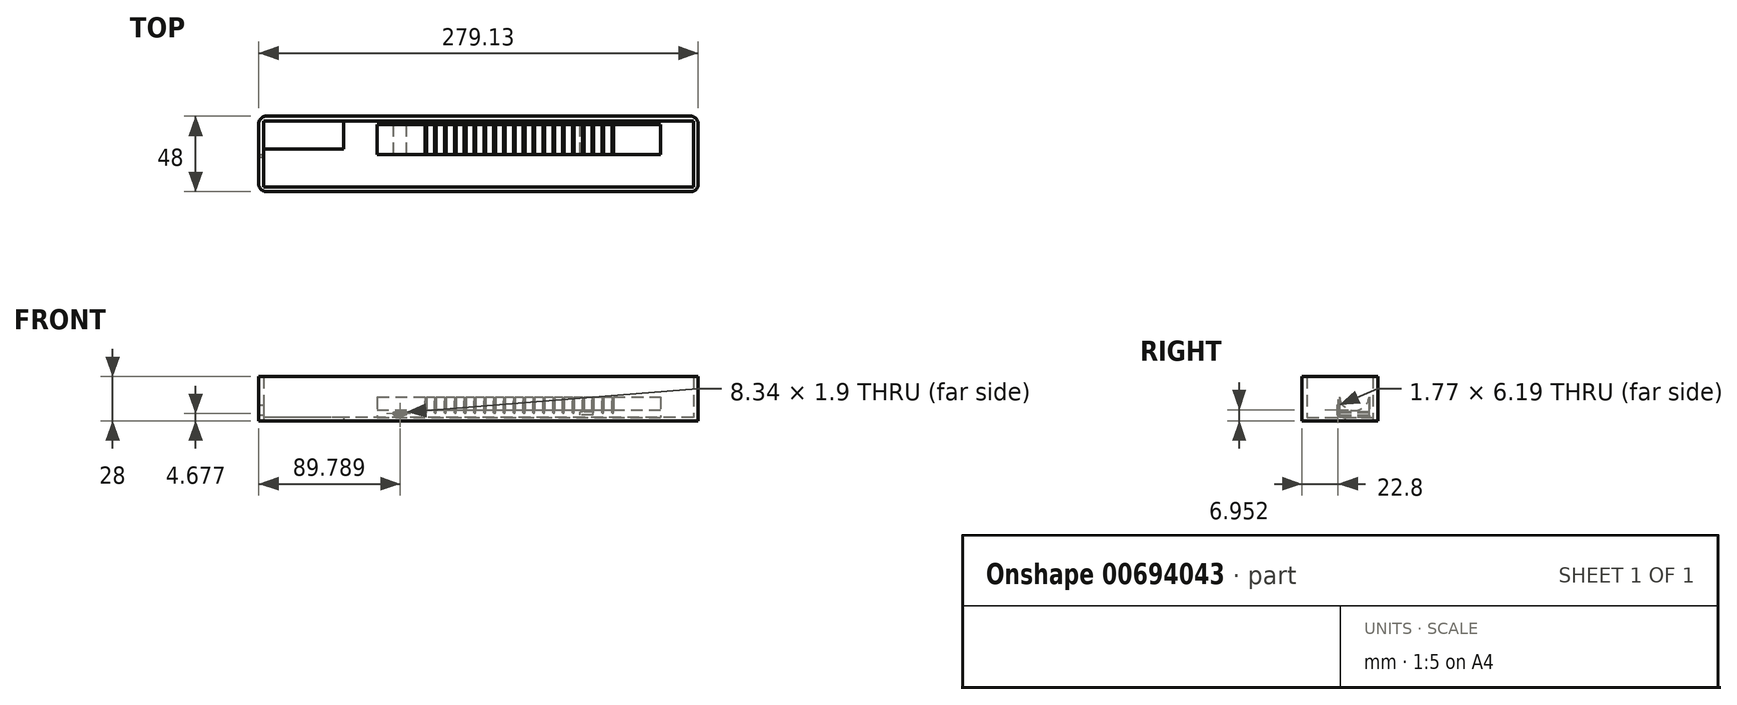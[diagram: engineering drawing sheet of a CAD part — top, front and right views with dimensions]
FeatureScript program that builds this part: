
annotation { "Feature Type Name" : "Feature", "Feature Type Description" : "" }
export const myFeature = defineFeature(function(context is Context, id is Id, definition is map)
    precondition{}
    {
        {
            var Q0;
            Q0=qCreatedBy(makeId("Top.planeOp"),FACE);
            var sketch = newSketch(context, id + "F0", { "sketchPlane" : qUnion([Q0])});
            skLineSegment(sketch, "E0.bottom", {"start": v(127.12, -24) * mm, "end": v(-146.01, -24) * mm});
            skLineSegment(sketch, "E0.top", {"start": v(127.12, 18) * mm, "end": v(-146.01, 18) * mm});
            skLineSegment(sketch, "E0.left", {"start": v(127.12, -24) * mm, "end": v(127.12, 18) * mm});
            skLineSegment(sketch, "E0.right", {"start": v(-146.01, -24) * mm, "end": v(-146.01, 18) * mm});
            skPoint(sketch, "E0.middle", {"position": v(0, 0) * mm});
            skLineSegment(sketch, "E1.bottom", {"start": v(-140.46, 74.6) * mm, "end": v(-84.46, 74.6) * mm});
            skLineSegment(sketch, "E1.top", {"start": v(-140.46, 108.6) * mm, "end": v(-84.46, 108.6) * mm});
            skLineSegment(sketch, "E1.left", {"start": v(-140.46, 74.6) * mm, "end": v(-140.46, 108.6) * mm});
            skLineSegment(sketch, "E1.right", {"start": v(-84.46, 74.6) * mm, "end": v(-84.46, 108.6) * mm});
            skLineSegment(sketch, "E2.0", {"start": v(-143.46, 111.6) * mm, "end": v(-81.46, 111.6) * mm, "construction": true});
            skLineSegment(sketch, "E2.1", {"start": v(-143.46, 71.6) * mm, "end": v(-143.46, 111.6) * mm, "construction": true});
            skLineSegment(sketch, "E2.2", {"start": v(-143.46, 71.6) * mm, "end": v(-81.46, 71.6) * mm, "construction": true});
            skLineSegment(sketch, "E2.3", {"start": v(-81.46, 71.6) * mm, "end": v(-81.46, 111.6) * mm, "construction": true});
            skLineSegment(sketch, "E3.bottom", {"start": v(-73.68, 15.64) * mm, "end": v(106.32, 15.64) * mm});
            skLineSegment(sketch, "E3.top", {"start": v(-73.68, -3.36) * mm, "end": v(106.32, -3.36) * mm});
            skLineSegment(sketch, "E3.left", {"start": v(-73.68, 15.64) * mm, "end": v(-73.68, -3.36) * mm});
            skLineSegment(sketch, "E3.right", {"start": v(106.32, 15.64) * mm, "end": v(106.32, -3.36) * mm});
            skLineSegment(sketch, "E4.bottom", {"start": v(96.3, 104.7) * mm, "end": v(145.3, 104.7) * mm, "construction": true});
            skLineSegment(sketch, "E4.top", {"start": v(96.3, 78.7) * mm, "end": v(145.3, 78.7) * mm, "construction": true});
            skLineSegment(sketch, "E4.left", {"start": v(96.3, 104.7) * mm, "end": v(96.3, 78.7) * mm, "construction": true});
            skLineSegment(sketch, "E4.right", {"start": v(145.3, 104.7) * mm, "end": v(145.3, 78.7) * mm, "construction": true});
            skLineSegment(sketch, "E5.0", {"start": v(91.3, 109.7) * mm, "end": v(150.3, 109.7) * mm, "construction": true});
            skLineSegment(sketch, "E5.1", {"start": v(91.3, 109.7) * mm, "end": v(91.3, 73.7) * mm, "construction": true});
            skLineSegment(sketch, "E5.2", {"start": v(91.3, 73.7) * mm, "end": v(150.3, 73.7) * mm, "construction": true});
            skLineSegment(sketch, "E5.3", {"start": v(150.3, 109.7) * mm, "end": v(150.3, 73.7) * mm, "construction": true});
            skLineSegment(sketch, "E6.0", {"start": v(130.12, 21) * mm, "end": v(-149.01, 21) * mm});
            skLineSegment(sketch, "E6.1", {"start": v(130.12, -27) * mm, "end": v(130.12, 21) * mm});
            skLineSegment(sketch, "E6.2", {"start": v(130.12, -27) * mm, "end": v(-149.01, -27) * mm});
            skLineSegment(sketch, "E6.3", {"start": v(-149.01, -27) * mm, "end": v(-149.01, 21) * mm});
            skLineSegment(sketch, "E7", {"start": v(-42.95, 15.64) * mm, "end": v(-42.95, -3.36) * mm});
            skLineSegment(sketch, "E8", {"start": v(-36.7, 15.64) * mm, "end": v(-36.7, -3.36) * mm});
            skLineSegment(sketch, "E9.1.0.0", {"start": v(-30.45, 15.64) * mm, "end": v(-30.45, -3.36) * mm});
            skLineSegment(sketch, "E9.1.0.1", {"start": v(-24.2, 15.64) * mm, "end": v(-24.2, -3.36) * mm});
            skLineSegment(sketch, "E9.2.0.0", {"start": v(-17.95, 15.64) * mm, "end": v(-17.95, -3.36) * mm});
            skLineSegment(sketch, "E9.2.0.1", {"start": v(-11.7, 15.64) * mm, "end": v(-11.7, -3.36) * mm});
            skLineSegment(sketch, "E9.3.0.0", {"start": v(-5.45, 15.64) * mm, "end": v(-5.45, -3.36) * mm});
            skLineSegment(sketch, "E9.3.0.1", {"start": v(0.8, 15.64) * mm, "end": v(0.8, -3.36) * mm});
            skLineSegment(sketch, "E9.4.0.0", {"start": v(7.05, 15.64) * mm, "end": v(7.05, -3.36) * mm});
            skLineSegment(sketch, "E9.4.0.1", {"start": v(13.3, 15.64) * mm, "end": v(13.3, -3.36) * mm});
            skLineSegment(sketch, "E9.5.0.0", {"start": v(19.55, 15.64) * mm, "end": v(19.55, -3.36) * mm});
            skLineSegment(sketch, "E9.5.0.1", {"start": v(25.8, 15.64) * mm, "end": v(25.8, -3.36) * mm});
            skLineSegment(sketch, "E9.6.0.0", {"start": v(32.05, 15.64) * mm, "end": v(32.05, -3.36) * mm});
            skLineSegment(sketch, "E9.6.0.1", {"start": v(38.3, 15.64) * mm, "end": v(38.3, -3.36) * mm});
            skLineSegment(sketch, "E9.7.0.0", {"start": v(44.55, 15.64) * mm, "end": v(44.55, -3.36) * mm});
            skLineSegment(sketch, "E9.7.0.1", {"start": v(50.8, 15.64) * mm, "end": v(50.8, -3.36) * mm});
            skLineSegment(sketch, "E9.8.0.0", {"start": v(57.05, 15.64) * mm, "end": v(57.05, -3.36) * mm});
            skLineSegment(sketch, "E9.8.0.1", {"start": v(63.3, 15.64) * mm, "end": v(63.3, -3.36) * mm});
            skLineSegment(sketch, "E9.9.0.0", {"start": v(69.55, 15.64) * mm, "end": v(69.55, -3.36) * mm});
            skLineSegment(sketch, "E9.9.0.1", {"start": v(75.8, 15.64) * mm, "end": v(75.8, -3.36) * mm});
            skLineSegment(sketch, "E9.direction1", {"start": v(-42.95, -3.36) * mm, "end": v(-30.45, -3.36) * mm, "construction": true});
            skLineSegment(sketch, "E10.bottom", {"start": v(-95.01, 0) * mm, "end": v(-146.01, 0) * mm});
            skLineSegment(sketch, "E10.top", {"start": v(-95.01, 18) * mm, "end": v(-146.01, 18) * mm});
            skLineSegment(sketch, "E10.left", {"start": v(-95.01, 0) * mm, "end": v(-95.01, 18) * mm});
            skLineSegment(sketch, "E11", {"start": v(-146.01, -3) * mm, "end": v(-92.01, -3) * mm});
            skLineSegment(sketch, "E12", {"start": v(-92.01, -3) * mm, "end": v(-92.01, 18) * mm});
            skLineSegment(sketch, "E13.0.left", {"start": v(-42.45, 15.64) * mm, "end": v(-42.45, -3.36) * mm});
            skLineSegment(sketch, "E13.0.right", {"start": v(-43.45, 15.64) * mm, "end": v(-43.45, -3.36) * mm});
            skLineSegment(sketch, "E14.0.left", {"start": v(-36.2, 15.64) * mm, "end": v(-36.2, -3.36) * mm});
            skLineSegment(sketch, "E14.0.right", {"start": v(-37.2, 15.64) * mm, "end": v(-37.2, -3.36) * mm});
            skLineSegment(sketch, "E15.2.0.0", {"start": v(-30.95, 15.64) * mm, "end": v(-30.95, -3.36) * mm});
            skLineSegment(sketch, "E15.2.0.2", {"start": v(-29.95, 15.64) * mm, "end": v(-29.95, -3.36) * mm});
            skLineSegment(sketch, "E15.3.0.0", {"start": v(-24.7, 15.64) * mm, "end": v(-24.7, -3.36) * mm});
            skLineSegment(sketch, "E15.3.0.2", {"start": v(-23.7, 15.64) * mm, "end": v(-23.7, -3.36) * mm});
            skLineSegment(sketch, "E15.4.0.0", {"start": v(-18.45, 15.64) * mm, "end": v(-18.45, -3.36) * mm});
            skLineSegment(sketch, "E15.4.0.2", {"start": v(-17.45, 15.64) * mm, "end": v(-17.45, -3.36) * mm});
            skLineSegment(sketch, "E15.5.0.0", {"start": v(-12.2, 15.64) * mm, "end": v(-12.2, -3.36) * mm});
            skLineSegment(sketch, "E15.5.0.2", {"start": v(-11.2, 15.64) * mm, "end": v(-11.2, -3.36) * mm});
            skLineSegment(sketch, "E15.6.0.0", {"start": v(-5.95, 15.64) * mm, "end": v(-5.95, -3.36) * mm});
            skLineSegment(sketch, "E15.6.0.2", {"start": v(-4.95, 15.64) * mm, "end": v(-4.95, -3.36) * mm});
            skLineSegment(sketch, "E15.7.0.0", {"start": v(0.3, 15.64) * mm, "end": v(0.3, -3.36) * mm});
            skLineSegment(sketch, "E15.7.0.2", {"start": v(1.3, 15.64) * mm, "end": v(1.3, -3.36) * mm});
            skLineSegment(sketch, "E15.8.0.0", {"start": v(6.55, 15.64) * mm, "end": v(6.55, -3.36) * mm});
            skLineSegment(sketch, "E15.8.0.2", {"start": v(7.55, 15.64) * mm, "end": v(7.55, -3.36) * mm});
            skLineSegment(sketch, "E15.9.0.0", {"start": v(12.8, 15.64) * mm, "end": v(12.8, -3.36) * mm});
            skLineSegment(sketch, "E15.9.0.2", {"start": v(13.8, 15.64) * mm, "end": v(13.8, -3.36) * mm});
            skLineSegment(sketch, "E15.10.0.0", {"start": v(19.05, 15.64) * mm, "end": v(19.05, -3.36) * mm});
            skLineSegment(sketch, "E15.10.0.2", {"start": v(20.05, 15.64) * mm, "end": v(20.05, -3.36) * mm});
            skLineSegment(sketch, "E15.11.0.0", {"start": v(25.3, 15.64) * mm, "end": v(25.3, -3.36) * mm});
            skLineSegment(sketch, "E15.11.0.2", {"start": v(26.3, 15.64) * mm, "end": v(26.3, -3.36) * mm});
            skLineSegment(sketch, "E15.12.0.0", {"start": v(31.55, 15.64) * mm, "end": v(31.55, -3.36) * mm});
            skLineSegment(sketch, "E15.12.0.2", {"start": v(32.55, 15.64) * mm, "end": v(32.55, -3.36) * mm});
            skLineSegment(sketch, "E15.13.0.0", {"start": v(37.8, 15.64) * mm, "end": v(37.8, -3.36) * mm});
            skLineSegment(sketch, "E15.13.0.2", {"start": v(38.8, 15.64) * mm, "end": v(38.8, -3.36) * mm});
            skLineSegment(sketch, "E15.14.0.0", {"start": v(44.05, 15.64) * mm, "end": v(44.05, -3.36) * mm});
            skLineSegment(sketch, "E15.14.0.2", {"start": v(45.05, 15.64) * mm, "end": v(45.05, -3.36) * mm});
            skLineSegment(sketch, "E15.15.0.0", {"start": v(50.3, 15.64) * mm, "end": v(50.3, -3.36) * mm});
            skLineSegment(sketch, "E15.15.0.2", {"start": v(51.3, 15.64) * mm, "end": v(51.3, -3.36) * mm});
            skLineSegment(sketch, "E15.16.0.0", {"start": v(56.55, 15.64) * mm, "end": v(56.55, -3.36) * mm});
            skLineSegment(sketch, "E15.16.0.2", {"start": v(57.55, 15.64) * mm, "end": v(57.55, -3.36) * mm});
            skLineSegment(sketch, "E15.17.0.0", {"start": v(62.8, 15.64) * mm, "end": v(62.8, -3.36) * mm});
            skLineSegment(sketch, "E15.17.0.2", {"start": v(63.8, 15.64) * mm, "end": v(63.8, -3.36) * mm});
            skLineSegment(sketch, "E15.18.0.0", {"start": v(69.05, 15.64) * mm, "end": v(69.05, -3.36) * mm});
            skLineSegment(sketch, "E15.18.0.2", {"start": v(70.05, 15.64) * mm, "end": v(70.05, -3.36) * mm});
            skLineSegment(sketch, "E15.19.0.0", {"start": v(75.3, 15.64) * mm, "end": v(75.3, -3.36) * mm});
            skLineSegment(sketch, "E15.19.0.2", {"start": v(76.3, 15.64) * mm, "end": v(76.3, -3.36) * mm});
            skLineSegment(sketch, "E15.direction1", {"start": v(-43.45, -3.36) * mm, "end": v(-37.2, -3.36) * mm, "construction": true});
            skLineSegment(sketch, "E16.bottom", {"start": v(-146.01, -8.98) * mm, "end": v(-139.7, -8.98) * mm});
            skLineSegment(sketch, "E16.top", {"start": v(-146.01, -11.97) * mm, "end": v(-139.7, -11.97) * mm});
            skLineSegment(sketch, "E16.left", {"start": v(-146.01, -8.98) * mm, "end": v(-146.01, -11.97) * mm});
            skLineSegment(sketch, "E16.right", {"start": v(-139.7, -8.98) * mm, "end": v(-139.7, -11.97) * mm});
            skLineSegment(sketch, "E17.bottom", {"start": v(-91.9, -9.3) * mm, "end": v(-98.5, -9.3) * mm});
            skLineSegment(sketch, "E17.top", {"start": v(-91.9, -12.28) * mm, "end": v(-98.5, -12.28) * mm});
            skLineSegment(sketch, "E17.left", {"start": v(-91.9, -9.3) * mm, "end": v(-91.9, -12.28) * mm});
            skLineSegment(sketch, "E17.right", {"start": v(-98.5, -9.3) * mm, "end": v(-98.5, -12.28) * mm});
            skSolve(sketch);
        }
        {
            var Q0;
            Q0=makeQuery(id+"F0.imprint","IMPRINT",FACE,{"disambiguationData":[TD([[makeQuery(id+"F0.imprint","IMPRINT",EDGE,{"derivedFrom":sQuery(id+"F0.wireOp",EDGE,"E3.bottom")}),-1.0]])]});
            extrude(context, id + "F1", {"entities" : qUnion([Q0]), "depth" : 15 * mm, "offsetDistance" : 25 * mm});
        }
        {
            var Q0;
            Q0=makeQuery(id+"F1.opExtrude","CAP_FACE",FACE,{"disambiguationData":[OSD([sQuery(id+"F0.wireOp",EDGE,"E3.bottom"),sQuery(id+"F0.wireOp",EDGE,"E3.top"),sQuery(id+"F0.wireOp",EDGE,"E3.left"),sQuery(id+"F0.wireOp",EDGE,"E3.right")])],"isStart":false});
            var sketch = newSketch(context, id + "F2", { "sketchPlane" : qUnion([Q0])});
            skLineSegment(sketch, "E18", {"start": v(-42.95, 15.64) * mm, "end": v(-42.95, -3.36) * mm});
            skLineSegment(sketch, "E19.0.left", {"start": v(-42.45, 15.64) * mm, "end": v(-42.45, -3.36) * mm});
            skLineSegment(sketch, "E19.0.right", {"start": v(-43.45, 15.64) * mm, "end": v(-43.45, -3.36) * mm});
            skLineSegment(sketch, "E20.1.0.0", {"start": v(-36.2, 15.64) * mm, "end": v(-36.2, -3.36) * mm});
            skLineSegment(sketch, "E20.1.0.1", {"start": v(-36.7, 15.64) * mm, "end": v(-36.7, -3.36) * mm});
            skLineSegment(sketch, "E20.1.0.2", {"start": v(-37.2, 15.64) * mm, "end": v(-37.2, -3.36) * mm});
            skLineSegment(sketch, "E20.2.0.0", {"start": v(-29.95, 15.64) * mm, "end": v(-29.95, -3.36) * mm});
            skLineSegment(sketch, "E20.2.0.1", {"start": v(-30.45, 15.64) * mm, "end": v(-30.45, -3.36) * mm});
            skLineSegment(sketch, "E20.2.0.2", {"start": v(-30.95, 15.64) * mm, "end": v(-30.95, -3.36) * mm});
            skLineSegment(sketch, "E20.3.0.0", {"start": v(-23.7, 15.64) * mm, "end": v(-23.7, -3.36) * mm});
            skLineSegment(sketch, "E20.3.0.1", {"start": v(-24.2, 15.64) * mm, "end": v(-24.2, -3.36) * mm});
            skLineSegment(sketch, "E20.3.0.2", {"start": v(-24.7, 15.64) * mm, "end": v(-24.7, -3.36) * mm});
            skLineSegment(sketch, "E20.4.0.0", {"start": v(-17.45, 15.64) * mm, "end": v(-17.45, -3.36) * mm});
            skLineSegment(sketch, "E20.4.0.1", {"start": v(-17.95, 15.64) * mm, "end": v(-17.95, -3.36) * mm});
            skLineSegment(sketch, "E20.4.0.2", {"start": v(-18.45, 15.64) * mm, "end": v(-18.45, -3.36) * mm});
            skLineSegment(sketch, "E20.5.0.0", {"start": v(-11.2, 15.64) * mm, "end": v(-11.2, -3.36) * mm});
            skLineSegment(sketch, "E20.5.0.1", {"start": v(-11.7, 15.64) * mm, "end": v(-11.7, -3.36) * mm});
            skLineSegment(sketch, "E20.5.0.2", {"start": v(-12.2, 15.64) * mm, "end": v(-12.2, -3.36) * mm});
            skLineSegment(sketch, "E20.6.0.0", {"start": v(-4.95, 15.64) * mm, "end": v(-4.95, -3.36) * mm});
            skLineSegment(sketch, "E20.6.0.1", {"start": v(-5.45, 15.64) * mm, "end": v(-5.45, -3.36) * mm});
            skLineSegment(sketch, "E20.6.0.2", {"start": v(-5.95, 15.64) * mm, "end": v(-5.95, -3.36) * mm});
            skLineSegment(sketch, "E20.7.0.0", {"start": v(1.3, 15.64) * mm, "end": v(1.3, -3.36) * mm});
            skLineSegment(sketch, "E20.7.0.1", {"start": v(0.8, 15.64) * mm, "end": v(0.8, -3.36) * mm});
            skLineSegment(sketch, "E20.7.0.2", {"start": v(0.3, 15.64) * mm, "end": v(0.3, -3.36) * mm});
            skLineSegment(sketch, "E20.8.0.0", {"start": v(7.55, 15.64) * mm, "end": v(7.55, -3.36) * mm});
            skLineSegment(sketch, "E20.8.0.1", {"start": v(7.05, 15.64) * mm, "end": v(7.05, -3.36) * mm});
            skLineSegment(sketch, "E20.8.0.2", {"start": v(6.55, 15.64) * mm, "end": v(6.55, -3.36) * mm});
            skLineSegment(sketch, "E20.9.0.0", {"start": v(13.8, 15.64) * mm, "end": v(13.8, -3.36) * mm});
            skLineSegment(sketch, "E20.9.0.1", {"start": v(13.3, 15.64) * mm, "end": v(13.3, -3.36) * mm});
            skLineSegment(sketch, "E20.9.0.2", {"start": v(12.8, 15.64) * mm, "end": v(12.8, -3.36) * mm});
            skLineSegment(sketch, "E20.10.0.0", {"start": v(20.05, 15.64) * mm, "end": v(20.05, -3.36) * mm});
            skLineSegment(sketch, "E20.10.0.1", {"start": v(19.55, 15.64) * mm, "end": v(19.55, -3.36) * mm});
            skLineSegment(sketch, "E20.10.0.2", {"start": v(19.05, 15.64) * mm, "end": v(19.05, -3.36) * mm});
            skLineSegment(sketch, "E20.11.0.0", {"start": v(26.3, 15.64) * mm, "end": v(26.3, -3.36) * mm});
            skLineSegment(sketch, "E20.11.0.1", {"start": v(25.8, 15.64) * mm, "end": v(25.8, -3.36) * mm});
            skLineSegment(sketch, "E20.11.0.2", {"start": v(25.3, 15.64) * mm, "end": v(25.3, -3.36) * mm});
            skLineSegment(sketch, "E20.12.0.0", {"start": v(32.55, 15.64) * mm, "end": v(32.55, -3.36) * mm});
            skLineSegment(sketch, "E20.12.0.1", {"start": v(32.05, 15.64) * mm, "end": v(32.05, -3.36) * mm});
            skLineSegment(sketch, "E20.12.0.2", {"start": v(31.55, 15.64) * mm, "end": v(31.55, -3.36) * mm});
            skLineSegment(sketch, "E20.13.0.0", {"start": v(38.8, 15.64) * mm, "end": v(38.8, -3.36) * mm});
            skLineSegment(sketch, "E20.13.0.1", {"start": v(38.3, 15.64) * mm, "end": v(38.3, -3.36) * mm});
            skLineSegment(sketch, "E20.13.0.2", {"start": v(37.8, 15.64) * mm, "end": v(37.8, -3.36) * mm});
            skLineSegment(sketch, "E20.14.0.0", {"start": v(45.05, 15.64) * mm, "end": v(45.05, -3.36) * mm});
            skLineSegment(sketch, "E20.14.0.1", {"start": v(44.55, 15.64) * mm, "end": v(44.55, -3.36) * mm});
            skLineSegment(sketch, "E20.14.0.2", {"start": v(44.05, 15.64) * mm, "end": v(44.05, -3.36) * mm});
            skLineSegment(sketch, "E20.15.0.0", {"start": v(51.3, 15.64) * mm, "end": v(51.3, -3.36) * mm});
            skLineSegment(sketch, "E20.15.0.1", {"start": v(50.8, 15.64) * mm, "end": v(50.8, -3.36) * mm});
            skLineSegment(sketch, "E20.15.0.2", {"start": v(50.3, 15.64) * mm, "end": v(50.3, -3.36) * mm});
            skLineSegment(sketch, "E20.16.0.0", {"start": v(57.55, 15.64) * mm, "end": v(57.55, -3.36) * mm});
            skLineSegment(sketch, "E20.16.0.1", {"start": v(57.05, 15.64) * mm, "end": v(57.05, -3.36) * mm});
            skLineSegment(sketch, "E20.16.0.2", {"start": v(56.55, 15.64) * mm, "end": v(56.55, -3.36) * mm});
            skLineSegment(sketch, "E20.17.0.0", {"start": v(63.8, 15.64) * mm, "end": v(63.8, -3.36) * mm});
            skLineSegment(sketch, "E20.17.0.1", {"start": v(63.3, 15.64) * mm, "end": v(63.3, -3.36) * mm});
            skLineSegment(sketch, "E20.17.0.2", {"start": v(62.8, 15.64) * mm, "end": v(62.8, -3.36) * mm});
            skLineSegment(sketch, "E20.18.0.0", {"start": v(70.05, 15.64) * mm, "end": v(70.05, -3.36) * mm});
            skLineSegment(sketch, "E20.18.0.1", {"start": v(69.55, 15.64) * mm, "end": v(69.55, -3.36) * mm});
            skLineSegment(sketch, "E20.18.0.2", {"start": v(69.05, 15.64) * mm, "end": v(69.05, -3.36) * mm});
            skLineSegment(sketch, "E20.19.0.0", {"start": v(76.3, 15.64) * mm, "end": v(76.3, -3.36) * mm});
            skLineSegment(sketch, "E20.19.0.1", {"start": v(75.8, 15.64) * mm, "end": v(75.8, -3.36) * mm});
            skLineSegment(sketch, "E20.19.0.2", {"start": v(75.3, 15.64) * mm, "end": v(75.3, -3.36) * mm});
            skLineSegment(sketch, "E20.direction1", {"start": v(-43.45, -3.36) * mm, "end": v(-37.2, -3.36) * mm, "construction": true});
            skSolve(sketch);
        }
        {
            var Q0;
            Q0=makeQuery(id+"F0.imprint","IMPRINT",FACE,{"disambiguationData":[TD([[makeQuery(id+"F0.imprint","IMPRINT",EDGE,{"derivedFrom":sQuery(id+"F0.wireOp",EDGE,"E0.bottom")}),-1.0]])]});
            var Q1;
            {var subQ0=sQuery(id+"F0.wireOp",EDGE,"E10.top");Q1=makeQuery(id+"F0.imprint","IMPRINT",FACE,{"disambiguationData":[TD([[makeQuery(id+"F0.imprint","IMPRINT",EDGE,{"derivedFrom":subQ0}),1.0]])]});}
            var Q2;
            {var subQ0=sQuery(id+"F0.wireOp",EDGE,"E10.bottom");Q2=makeQuery(id+"F0.imprint","IMPRINT",FACE,{"disambiguationData":[TD([[makeQuery(id+"F0.imprint","IMPRINT",EDGE,{"derivedFrom":subQ0}),1.0]])]});}
            var Q3;
            Q3=makeQuery(id+"F0.imprint","IMPRINT",FACE,{"disambiguationData":[TD([[makeQuery(id+"F0.imprint","IMPRINT",EDGE,{"derivedFrom":sQuery(id+"F0.wireOp",EDGE,"E16.bottom")}),-1.0]])]});
            var Q4;
            Q4=makeQuery(id+"F0.imprint","IMPRINT",FACE,{"disambiguationData":[TD([[makeQuery(id+"F0.imprint","IMPRINT",EDGE,{"derivedFrom":sQuery(id+"F0.wireOp",EDGE,"E17.bottom")}),1.0]])]});
            extrude(context, id + "F3", {"entities" : qUnion([Q0, Q1, Q2, Q3, Q4]), "operationType" : NewBodyOperationType.ADD, "depth" : 2 * mm, "offsetDistance" : 25 * mm});
        }
        {
            var Q0;
            Q0=makeQuery(id+"F1.opExtrude","SWEPT_FACE",FACE,{"disambiguationData":[OSD([sQuery(id+"F0.wireOp",EDGE,"E3.left")])]});
            var sketch = newSketch(context, id + "F4", { "sketchPlane" : qUnion([Q0])});
            skCircle(sketch, "E21", {"center": v(-6.14, 16) * mm, "radius": 9.5 * mm});
            skPoint(sketch, "E22", {"position": v(-6.14, 2) * mm});
            skLineSegment(sketch, "E23", {"start": v(-6.14, 2) * mm, "end": v(-6.14, 20.98) * mm, "construction": true});
            skSolve(sketch);
        }
        {
            var Q0;
            Q0 = qSketchRegion(id + "F4", true);
            extrude(context, id + "F5", {"entities" : qUnion([Q0]), "operationType" : NewBodyOperationType.REMOVE, "oppositeDirection" : true, "depth" : 180 * mm, "offsetDistance" : 25 * mm});
        }
        {
            var Q0;
            Q0=makeQuery(id+"F1.opExtrude","SWEPT_FACE",FACE,{"disambiguationData":[OSD([sQuery(id+"F0.wireOp",EDGE,"E3.bottom")])]});
            var sketch = newSketch(context, id + "F6", { "sketchPlane" : qUnion([Q0])});
            skLineSegment(sketch, "E24.bottom", {"start": v(-63.4, 3.73) * mm, "end": v(-55.05, 3.73) * mm});
            skLineSegment(sketch, "E24.top", {"start": v(-63.4, 5.63) * mm, "end": v(-55.05, 5.63) * mm});
            skLineSegment(sketch, "E24.left", {"start": v(-63.4, 3.73) * mm, "end": v(-63.4, 5.63) * mm});
            skLineSegment(sketch, "E24.right", {"start": v(-55.05, 3.73) * mm, "end": v(-55.05, 5.63) * mm});
            skLineSegment(sketch, "E25.MirrorCS", {"start": v(63.4, 5.63) * mm, "end": v(55.05, 5.63) * mm});
            skLineSegment(sketch, "E26.MirrorCS", {"start": v(63.4, 3.73) * mm, "end": v(55.05, 3.73) * mm});
            skLineSegment(sketch, "E27.MirrorCS", {"start": v(55.05, 3.73) * mm, "end": v(55.05, 5.63) * mm});
            skLineSegment(sketch, "E28.MirrorCS", {"start": v(63.4, 3.73) * mm, "end": v(63.4, 5.63) * mm});
            skSolve(sketch);
        }
        {
            var Q0;
            {var subQ0=sQuery(id+"F2.wireOp",EDGE,"E18");Q0=makeQuery(id+"F2.imprint","IMPRINT",FACE,{"disambiguationData":[TD([[makeQuery(id+"F2.imprint","IMPRINT",EDGE,{"derivedFrom":subQ0}),-1.0]])]});}
            var Q1;
            {var subQ0=sQuery(id+"F2.wireOp",EDGE,"E18");Q1=makeQuery(id+"F2.imprint","IMPRINT",FACE,{"disambiguationData":[TD([[makeQuery(id+"F2.imprint","IMPRINT",EDGE,{"derivedFrom":subQ0}),1.0]])]});}
            var Q2;
            {var subQ0=sQuery(id+"F2.wireOp",EDGE,"E20.1.0.1");Q2=makeQuery(id+"F2.imprint","IMPRINT",FACE,{"disambiguationData":[TD([[makeQuery(id+"F2.imprint","IMPRINT",EDGE,{"derivedFrom":subQ0}),-1.0]])]});}
            var Q3;
            {var subQ0=sQuery(id+"F2.wireOp",EDGE,"E20.1.0.0");Q3=makeQuery(id+"F2.imprint","IMPRINT",FACE,{"disambiguationData":[TD([[makeQuery(id+"F2.imprint","IMPRINT",EDGE,{"derivedFrom":subQ0}),-1.0]])]});}
            var Q4;
            {var subQ0=sQuery(id+"F2.wireOp",EDGE,"E20.2.0.1");Q4=makeQuery(id+"F2.imprint","IMPRINT",FACE,{"disambiguationData":[TD([[makeQuery(id+"F2.imprint","IMPRINT",EDGE,{"derivedFrom":subQ0}),-1.0]])]});}
            var Q5;
            {var subQ0=sQuery(id+"F2.wireOp",EDGE,"E20.2.0.0");Q5=makeQuery(id+"F2.imprint","IMPRINT",FACE,{"disambiguationData":[TD([[makeQuery(id+"F2.imprint","IMPRINT",EDGE,{"derivedFrom":subQ0}),-1.0]])]});}
            var Q6;
            {var subQ0=sQuery(id+"F2.wireOp",EDGE,"E20.3.0.1");Q6=makeQuery(id+"F2.imprint","IMPRINT",FACE,{"disambiguationData":[TD([[makeQuery(id+"F2.imprint","IMPRINT",EDGE,{"derivedFrom":subQ0}),-1.0]])]});}
            var Q7;
            {var subQ0=sQuery(id+"F2.wireOp",EDGE,"E20.3.0.0");Q7=makeQuery(id+"F2.imprint","IMPRINT",FACE,{"disambiguationData":[TD([[makeQuery(id+"F2.imprint","IMPRINT",EDGE,{"derivedFrom":subQ0}),-1.0]])]});}
            var Q8;
            {var subQ0=sQuery(id+"F2.wireOp",EDGE,"E20.4.0.1");Q8=makeQuery(id+"F2.imprint","IMPRINT",FACE,{"disambiguationData":[TD([[makeQuery(id+"F2.imprint","IMPRINT",EDGE,{"derivedFrom":subQ0}),-1.0]])]});}
            var Q9;
            {var subQ0=sQuery(id+"F2.wireOp",EDGE,"E20.4.0.0");Q9=makeQuery(id+"F2.imprint","IMPRINT",FACE,{"disambiguationData":[TD([[makeQuery(id+"F2.imprint","IMPRINT",EDGE,{"derivedFrom":subQ0}),-1.0]])]});}
            var Q10;
            {var subQ0=sQuery(id+"F2.wireOp",EDGE,"E20.5.0.1");Q10=makeQuery(id+"F2.imprint","IMPRINT",FACE,{"disambiguationData":[TD([[makeQuery(id+"F2.imprint","IMPRINT",EDGE,{"derivedFrom":subQ0}),-1.0]])]});}
            var Q11;
            {var subQ0=sQuery(id+"F2.wireOp",EDGE,"E20.5.0.0");Q11=makeQuery(id+"F2.imprint","IMPRINT",FACE,{"disambiguationData":[TD([[makeQuery(id+"F2.imprint","IMPRINT",EDGE,{"derivedFrom":subQ0}),-1.0]])]});}
            var Q12;
            {var subQ0=sQuery(id+"F2.wireOp",EDGE,"E20.6.0.1");Q12=makeQuery(id+"F2.imprint","IMPRINT",FACE,{"disambiguationData":[TD([[makeQuery(id+"F2.imprint","IMPRINT",EDGE,{"derivedFrom":subQ0}),-1.0]])]});}
            var Q13;
            {var subQ0=sQuery(id+"F2.wireOp",EDGE,"E20.6.0.0");Q13=makeQuery(id+"F2.imprint","IMPRINT",FACE,{"disambiguationData":[TD([[makeQuery(id+"F2.imprint","IMPRINT",EDGE,{"derivedFrom":subQ0}),-1.0]])]});}
            var Q14;
            {var subQ0=sQuery(id+"F2.wireOp",EDGE,"E20.7.0.1");Q14=makeQuery(id+"F2.imprint","IMPRINT",FACE,{"disambiguationData":[TD([[makeQuery(id+"F2.imprint","IMPRINT",EDGE,{"derivedFrom":subQ0}),-1.0]])]});}
            var Q15;
            {var subQ0=sQuery(id+"F2.wireOp",EDGE,"E20.7.0.0");Q15=makeQuery(id+"F2.imprint","IMPRINT",FACE,{"disambiguationData":[TD([[makeQuery(id+"F2.imprint","IMPRINT",EDGE,{"derivedFrom":subQ0}),-1.0]])]});}
            var Q16;
            {var subQ0=sQuery(id+"F2.wireOp",EDGE,"E20.8.0.1");Q16=makeQuery(id+"F2.imprint","IMPRINT",FACE,{"disambiguationData":[TD([[makeQuery(id+"F2.imprint","IMPRINT",EDGE,{"derivedFrom":subQ0}),-1.0]])]});}
            var Q17;
            {var subQ0=sQuery(id+"F2.wireOp",EDGE,"E20.8.0.0");Q17=makeQuery(id+"F2.imprint","IMPRINT",FACE,{"disambiguationData":[TD([[makeQuery(id+"F2.imprint","IMPRINT",EDGE,{"derivedFrom":subQ0}),-1.0]])]});}
            var Q18;
            {var subQ0=sQuery(id+"F2.wireOp",EDGE,"E20.9.0.1");Q18=makeQuery(id+"F2.imprint","IMPRINT",FACE,{"disambiguationData":[TD([[makeQuery(id+"F2.imprint","IMPRINT",EDGE,{"derivedFrom":subQ0}),-1.0]])]});}
            var Q19;
            {var subQ0=sQuery(id+"F2.wireOp",EDGE,"E20.9.0.0");Q19=makeQuery(id+"F2.imprint","IMPRINT",FACE,{"disambiguationData":[TD([[makeQuery(id+"F2.imprint","IMPRINT",EDGE,{"derivedFrom":subQ0}),-1.0]])]});}
            var Q20;
            {var subQ0=sQuery(id+"F2.wireOp",EDGE,"E20.10.0.1");Q20=makeQuery(id+"F2.imprint","IMPRINT",FACE,{"disambiguationData":[TD([[makeQuery(id+"F2.imprint","IMPRINT",EDGE,{"derivedFrom":subQ0}),-1.0]])]});}
            var Q21;
            {var subQ0=sQuery(id+"F2.wireOp",EDGE,"E20.10.0.0");Q21=makeQuery(id+"F2.imprint","IMPRINT",FACE,{"disambiguationData":[TD([[makeQuery(id+"F2.imprint","IMPRINT",EDGE,{"derivedFrom":subQ0}),-1.0]])]});}
            var Q22;
            {var subQ0=sQuery(id+"F2.wireOp",EDGE,"E20.11.0.1");Q22=makeQuery(id+"F2.imprint","IMPRINT",FACE,{"disambiguationData":[TD([[makeQuery(id+"F2.imprint","IMPRINT",EDGE,{"derivedFrom":subQ0}),-1.0]])]});}
            var Q23;
            {var subQ0=sQuery(id+"F2.wireOp",EDGE,"E20.11.0.0");Q23=makeQuery(id+"F2.imprint","IMPRINT",FACE,{"disambiguationData":[TD([[makeQuery(id+"F2.imprint","IMPRINT",EDGE,{"derivedFrom":subQ0}),-1.0]])]});}
            var Q24;
            {var subQ0=sQuery(id+"F2.wireOp",EDGE,"E20.12.0.1");Q24=makeQuery(id+"F2.imprint","IMPRINT",FACE,{"disambiguationData":[TD([[makeQuery(id+"F2.imprint","IMPRINT",EDGE,{"derivedFrom":subQ0}),-1.0]])]});}
            var Q25;
            {var subQ0=sQuery(id+"F2.wireOp",EDGE,"E20.12.0.0");Q25=makeQuery(id+"F2.imprint","IMPRINT",FACE,{"disambiguationData":[TD([[makeQuery(id+"F2.imprint","IMPRINT",EDGE,{"derivedFrom":subQ0}),-1.0]])]});}
            var Q26;
            {var subQ0=sQuery(id+"F2.wireOp",EDGE,"E20.13.0.1");Q26=makeQuery(id+"F2.imprint","IMPRINT",FACE,{"disambiguationData":[TD([[makeQuery(id+"F2.imprint","IMPRINT",EDGE,{"derivedFrom":subQ0}),-1.0]])]});}
            var Q27;
            {var subQ0=sQuery(id+"F2.wireOp",EDGE,"E20.13.0.0");Q27=makeQuery(id+"F2.imprint","IMPRINT",FACE,{"disambiguationData":[TD([[makeQuery(id+"F2.imprint","IMPRINT",EDGE,{"derivedFrom":subQ0}),-1.0]])]});}
            var Q28;
            {var subQ0=sQuery(id+"F2.wireOp",EDGE,"E20.14.0.1");Q28=makeQuery(id+"F2.imprint","IMPRINT",FACE,{"disambiguationData":[TD([[makeQuery(id+"F2.imprint","IMPRINT",EDGE,{"derivedFrom":subQ0}),-1.0]])]});}
            var Q29;
            {var subQ0=sQuery(id+"F2.wireOp",EDGE,"E20.14.0.0");Q29=makeQuery(id+"F2.imprint","IMPRINT",FACE,{"disambiguationData":[TD([[makeQuery(id+"F2.imprint","IMPRINT",EDGE,{"derivedFrom":subQ0}),-1.0]])]});}
            var Q30;
            {var subQ0=sQuery(id+"F2.wireOp",EDGE,"E20.15.0.1");Q30=makeQuery(id+"F2.imprint","IMPRINT",FACE,{"disambiguationData":[TD([[makeQuery(id+"F2.imprint","IMPRINT",EDGE,{"derivedFrom":subQ0}),-1.0]])]});}
            var Q31;
            {var subQ0=sQuery(id+"F2.wireOp",EDGE,"E20.15.0.0");Q31=makeQuery(id+"F2.imprint","IMPRINT",FACE,{"disambiguationData":[TD([[makeQuery(id+"F2.imprint","IMPRINT",EDGE,{"derivedFrom":subQ0}),-1.0]])]});}
            var Q32;
            {var subQ0=sQuery(id+"F2.wireOp",EDGE,"E20.16.0.1");Q32=makeQuery(id+"F2.imprint","IMPRINT",FACE,{"disambiguationData":[TD([[makeQuery(id+"F2.imprint","IMPRINT",EDGE,{"derivedFrom":subQ0}),-1.0]])]});}
            var Q33;
            {var subQ0=sQuery(id+"F2.wireOp",EDGE,"E20.16.0.0");Q33=makeQuery(id+"F2.imprint","IMPRINT",FACE,{"disambiguationData":[TD([[makeQuery(id+"F2.imprint","IMPRINT",EDGE,{"derivedFrom":subQ0}),-1.0]])]});}
            var Q34;
            {var subQ0=sQuery(id+"F2.wireOp",EDGE,"E20.17.0.1");Q34=makeQuery(id+"F2.imprint","IMPRINT",FACE,{"disambiguationData":[TD([[makeQuery(id+"F2.imprint","IMPRINT",EDGE,{"derivedFrom":subQ0}),-1.0]])]});}
            var Q35;
            {var subQ0=sQuery(id+"F2.wireOp",EDGE,"E20.17.0.0");Q35=makeQuery(id+"F2.imprint","IMPRINT",FACE,{"disambiguationData":[TD([[makeQuery(id+"F2.imprint","IMPRINT",EDGE,{"derivedFrom":subQ0}),-1.0]])]});}
            var Q36;
            {var subQ0=sQuery(id+"F2.wireOp",EDGE,"E20.18.0.1");Q36=makeQuery(id+"F2.imprint","IMPRINT",FACE,{"disambiguationData":[TD([[makeQuery(id+"F2.imprint","IMPRINT",EDGE,{"derivedFrom":subQ0}),-1.0]])]});}
            var Q37;
            {var subQ0=sQuery(id+"F2.wireOp",EDGE,"E20.18.0.0");Q37=makeQuery(id+"F2.imprint","IMPRINT",FACE,{"disambiguationData":[TD([[makeQuery(id+"F2.imprint","IMPRINT",EDGE,{"derivedFrom":subQ0}),-1.0]])]});}
            var Q38;
            {var subQ0=sQuery(id+"F2.wireOp",EDGE,"E20.19.0.1");Q38=makeQuery(id+"F2.imprint","IMPRINT",FACE,{"disambiguationData":[TD([[makeQuery(id+"F2.imprint","IMPRINT",EDGE,{"derivedFrom":subQ0}),-1.0]])]});}
            var Q39;
            {var subQ0=sQuery(id+"F2.wireOp",EDGE,"E20.19.0.0");Q39=makeQuery(id+"F2.imprint","IMPRINT",FACE,{"disambiguationData":[TD([[makeQuery(id+"F2.imprint","IMPRINT",EDGE,{"derivedFrom":subQ0}),-1.0]])]});}
            extrude(context, id + "F7", {"entities" : qUnion([Q0, Q1, Q2, Q3, Q4, Q5, Q6, Q7, Q8, Q9, Q10, Q11, Q12, Q13, Q14, Q15, Q16, Q17, Q18, Q19, Q20, Q21, Q22, Q23, Q24, Q25, Q26, Q27, Q28, Q29, Q30, Q31, Q32, Q33, Q34, Q35, Q36, Q37, Q38, Q39]), "operationType" : NewBodyOperationType.REMOVE, "oppositeDirection" : true, "depth" : 10 * mm, "offsetDistance" : 25 * mm});
        }
        {
            var Q0;
            Q0 = qSketchRegion(id + "F6", true);
            extrude(context, id + "F8", {"entities" : qUnion([Q0]), "operationType" : NewBodyOperationType.REMOVE, "oppositeDirection" : true, "depth" : 19 * mm, "offsetDistance" : 25 * mm});
        }
        {
            var Q0;
            Q0=makeQuery(id+"F0.imprint","IMPRINT",FACE,{"disambiguationData":[TD([[makeQuery(id+"F0.imprint","IMPRINT",EDGE,{"derivedFrom":sQuery(id+"F0.wireOp",EDGE,"E0.bottom")}),1.0]])]});
            extrude(context, id + "F9", {"entities" : qUnion([Q0]), "operationType" : NewBodyOperationType.ADD, "depth" : 28 * mm, "offsetDistance" : 25 * mm});
        }
        {
            var Q0;
            Q0=makeQuery(id+"F9.opExtrude","SWEPT_FACE",FACE,{"disambiguationData":[OSD([sQuery(id+"F0.wireOp",EDGE,"E6.3")])]});
            var sketch = newSketch(context, id + "F10", { "sketchPlane" : qUnion([Q0])});
            skLineSegment(sketch, "E29.bottom", {"start": v(3.32, 3.86) * mm, "end": v(5.09, 3.86) * mm});
            skLineSegment(sketch, "E29.top", {"start": v(3.32, 10.05) * mm, "end": v(5.09, 10.05) * mm});
            skLineSegment(sketch, "E29.left", {"start": v(3.32, 3.86) * mm, "end": v(3.32, 10.05) * mm});
            skLineSegment(sketch, "E29.right", {"start": v(5.09, 3.86) * mm, "end": v(5.09, 10.05) * mm});
            skSolve(sketch);
        }
        {
            var Q0;
            Q0=makeQuery(id+"F10.imprint","IMPRINT",FACE,{"disambiguationData":[TD([[makeQuery(id+"F10.imprint","IMPRINT",EDGE,{"derivedFrom":sQuery(id+"F10.wireOp",EDGE,"0C9LDvGU-AvFy-jFwl-X3u2-vlHjBjzznu7Y.bottom")}),-1.0]])]});
            var Q1;
            Q1=makeQuery(id+"F10.imprint","IMPRINT",FACE,{"disambiguationData":[TD([[makeQuery(id+"F10.imprint","IMPRINT",EDGE,{"derivedFrom":sQuery(id+"F10.wireOp",EDGE,"E29.bottom")}),1.0]])]});
            extrude(context, id + "F11", {"entities" : qUnion([Q0, Q1]), "operationType" : NewBodyOperationType.REMOVE, "endBound" : BoundingType.SYMMETRIC, "depth" : 10 * mm, "offsetDistance" : 25 * mm});
        }
        {
            var Q0;
            Q0=makeQuery(id+"F9.opExtrude","SWEPT_EDGE",EDGE,{"disambiguationData":[OSD([sQuery(id+"F0.wireOp",EDGE,"E6.0"),sQuery(id+"F0.wireOp",EDGE,"E6.3")])]});
            var Q1;
            Q1=makeQuery(id+"F9.opExtrude","SWEPT_EDGE",EDGE,{"disambiguationData":[OSD([sQuery(id+"F0.wireOp",EDGE,"E6.0"),sQuery(id+"F0.wireOp",EDGE,"E6.1")])]});
            var Q2;
            Q2=makeQuery(id+"F9.opExtrude","SWEPT_EDGE",EDGE,{"disambiguationData":[OSD([sQuery(id+"F0.wireOp",EDGE,"E6.2"),sQuery(id+"F0.wireOp",EDGE,"E6.3")])]});
            var Q3;
            Q3=makeQuery(id+"F9.opExtrude","SWEPT_EDGE",EDGE,{"disambiguationData":[OSD([sQuery(id+"F0.wireOp",EDGE,"E6.1"),sQuery(id+"F0.wireOp",EDGE,"E6.2")])]});
            fillet(context, id + "F12", {"entities" : qUnion([Q0, Q1, Q2, Q3]), "radius" : 5 * mm, "tangentPropagation" : true, "allowEdgeOverflow" : false});
        }
    });
